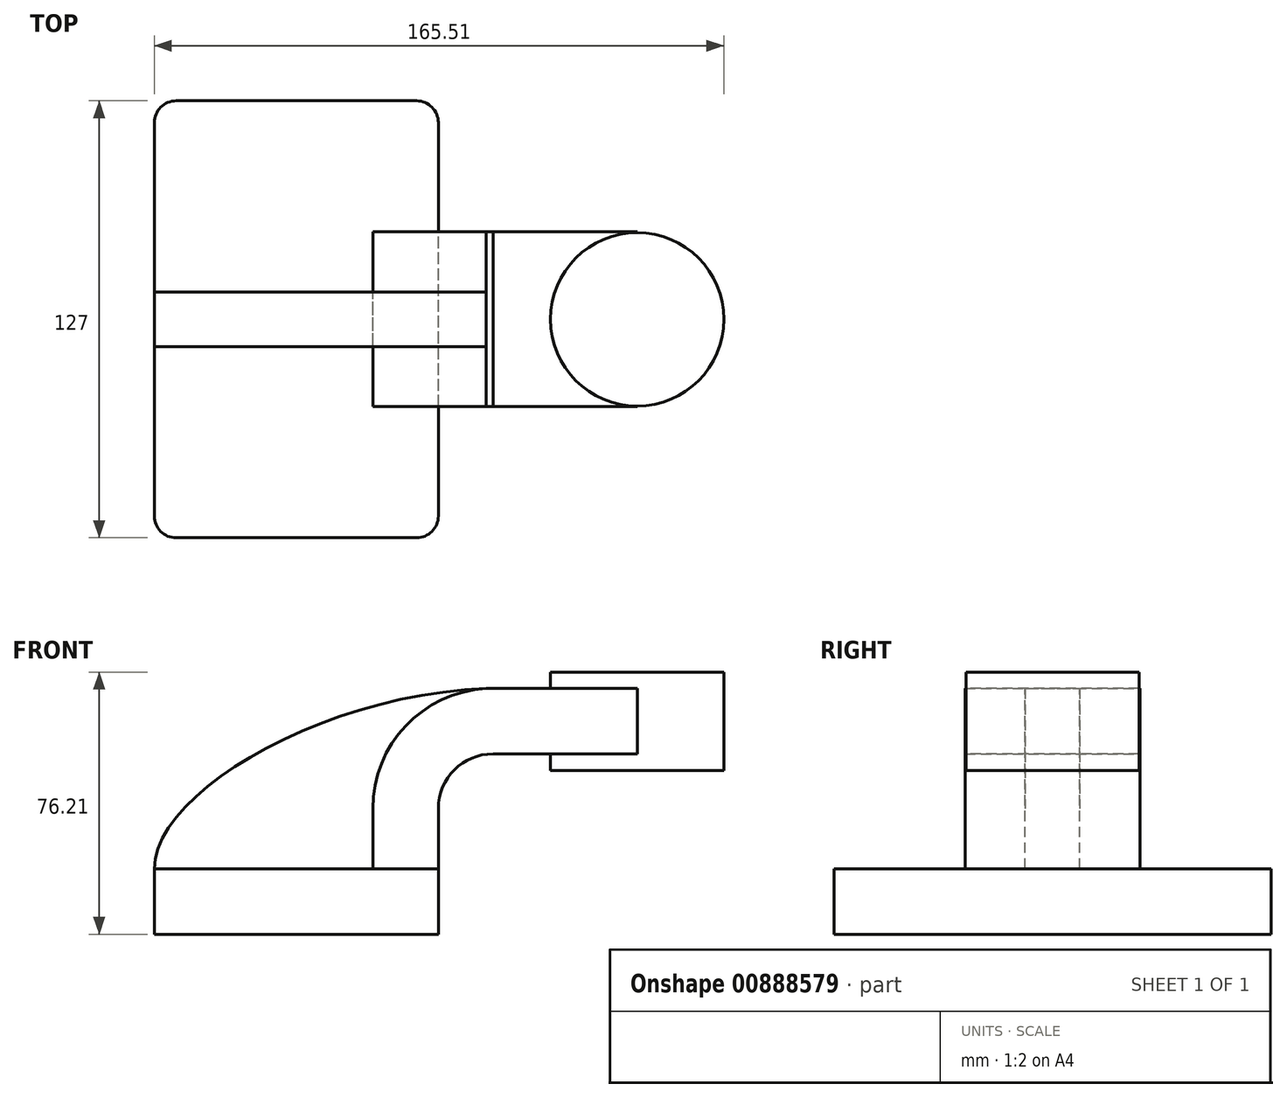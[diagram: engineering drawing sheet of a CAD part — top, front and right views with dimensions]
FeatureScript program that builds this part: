
annotation { "Feature Type Name" : "Feature", "Feature Type Description" : "" }
export const myFeature = defineFeature(function(context is Context, id is Id, definition is map)
    precondition{}
    {
        {
            var Q0;
            Q0=qCreatedBy(makeId("Front.planeOp"),FACE);
            var sketch = newSketch(context, id + "F0", { "sketchPlane" : qUnion([Q0])});
            skLineSegment(sketch, "E0.bottom", {"start": v(-41.28, 9.52) * mm, "end": v(41.27, 9.53) * mm});
            skLineSegment(sketch, "E0.top", {"start": v(-41.28, -9.53) * mm, "end": v(41.28, -9.53) * mm});
            skLineSegment(sketch, "E0.left", {"start": v(-41.28, 9.52) * mm, "end": v(-41.27, -9.53) * mm});
            skLineSegment(sketch, "E0.right", {"start": v(41.28, 9.53) * mm, "end": v(41.28, -9.52) * mm});
            skPoint(sketch, "E0.middle", {"position": v(0, 0) * mm});
            skLineSegment(sketch, "E1.bottom", {"start": v(73.43, 38.1) * mm, "end": v(124.23, 38.1) * mm});
            skLineSegment(sketch, "E1.top", {"start": v(73.43, 66.67) * mm, "end": v(124.23, 66.67) * mm});
            skLineSegment(sketch, "E1.left", {"start": v(73.43, 38.1) * mm, "end": v(73.43, 66.67) * mm});
            skLineSegment(sketch, "E1.right", {"start": v(124.23, 38.1) * mm, "end": v(124.23, 66.67) * mm});
            skPoint(sketch, "E1.middle", {"position": v(98.83, 52.39) * mm});
            skLineSegment(sketch, "E2", {"start": v(41.27, 9.53) * mm, "end": v(41.27, 27) * mm});
            skArc(sketch, "E3", {"start": v(41.27, 27) * mm, "mid": v(45.92, 38.23) * mm, "end": v(57.15, 42.88) * mm});
            skLineSegment(sketch, "E4", {"start": v(57.15, 42.88) * mm, "end": v(99.04, 42.88) * mm});
            skLineSegment(sketch, "E5.0", {"start": v(57.15, 61.93) * mm, "end": v(99.04, 61.93) * mm});
            skArc(sketch, "E5.1", {"start": v(22.22, 27) * mm, "mid": v(32.45, 51.7) * mm, "end": v(57.15, 61.93) * mm});
            skLineSegment(sketch, "E5.2", {"start": v(22.22, 9.53) * mm, "end": v(22.22, 27) * mm});
            skLineSegment(sketch, "E6", {"start": v(99.04, 66.67) * mm, "end": v(99.04, 38.1) * mm});
            skFitSpline(sketch, "E7", {"points": [v(-41.28, 9.52) * mm, v(57.15, 61.93) * mm], "startDerivative": vector(0.2, 66.62) * mm, "endDerivative": vector(146.2, 3.05) * mm});
            skSolve(sketch);
        }
        {
            var Q0;
            Q0=makeQuery(id+"F0.imprint","IMPRINT",FACE,{"disambiguationData":[TD([[makeQuery(id+"F0.imprint","IMPRINT",EDGE,{"derivedFrom":sQuery(id+"F0.wireOp",EDGE,"E0.top")}),1.0]])]});
            extrude(context, id + "F1", {"entities" : qUnion([Q0]), "endBound" : BoundingType.SYMMETRIC, "depth" : 127 * mm, "offsetDistance" : 25.4 * mm});
        }
        {
            var Q0;
            {var subQ1=sQuery(id+"F0.wireOp",EDGE,"E2");Q0=makeQuery(id+"F0.imprint","IMPRINT",FACE,{"disambiguationData":[TD([[makeQuery(id+"F0.imprint","IMPRINT",EDGE,{"derivedFrom":subQ1}),1.0]])]});}
            var Q1;
            {var subQ0=sQuery(id+"F0.wireOp",EDGE,"E4");var subQ1=sQuery(id+"F0.wireOp",EDGE,"E1.left");var subQ2=makeQuery(id+"F0.imprint","INTERSECT",VERTEX,{"derivedFrom":[subQ1,subQ0]});Q1=makeQuery(id+"F0.imprint","IMPRINT",FACE,{"disambiguationData":[TD([[makeQuery(id+"F0.imprint","IMPRINT",EDGE,{"disambiguationData":[TD([[subQ2,-1.0]])],"derivedFrom":subQ1}),-1.0]])]});}
            extrude(context, id + "F2", {"entities" : qUnion([Q0, Q1]), "endBound" : BoundingType.SYMMETRIC, "depth" : 50.8 * mm, "offsetDistance" : 25.4 * mm});
        }
        {
            var Q0;
            {var subQ3=sQuery(id+"F0.wireOp",EDGE,"E5.2");Q0=makeQuery(id+"F0.imprint","IMPRINT",FACE,{"disambiguationData":[TD([[makeQuery(id+"F0.imprint","IMPRINT",EDGE,{"derivedFrom":subQ3}),1.0]])]});}
            extrude(context, id + "F3", {"entities" : qUnion([Q0]), "endBound" : BoundingType.SYMMETRIC, "depth" : 15.88 * mm, "offsetDistance" : 25.4 * mm});
        }
        {
            var Q0;
            {var subQ4=sQuery(id+"F0.wireOp",EDGE,"E1.right");Q0=makeQuery(id+"F0.imprint","IMPRINT",FACE,{"disambiguationData":[TD([[makeQuery(id+"F0.imprint","IMPRINT",EDGE,{"derivedFrom":subQ4}),1.0]])]});}
            var Q1;
            Q1=sQuery(id+"F0.wireOp",EDGE,"E6");
            revolve(context, id + "F4", {"operationType" : NewBodyOperationType.ADD, "surfaceOperationType" : NewSurfaceOperationType.NEW, "entities" : qUnion([Q0]), "axis" : qUnion([Q1]), "revolveType" : RevolveType.FULL});
        }
        {
            var Q0;
            Q0=makeQuery(id+"F1.opExtrude","CAP_EDGE",EDGE,{"disambiguationData":[OSD([sQuery(id+"F0.wireOp",EDGE,"E0.left")])],"isStart":false});
            var Q1;
            Q1=makeQuery(id+"F1.opExtrude","CAP_EDGE",EDGE,{"disambiguationData":[OSD([sQuery(id+"F0.wireOp",EDGE,"E0.right")])],"isStart":false});
            var Q2;
            Q2=makeQuery(id+"F1.opExtrude","CAP_EDGE",EDGE,{"disambiguationData":[OSD([sQuery(id+"F0.wireOp",EDGE,"E0.right")])],"isStart":true});
            var Q3;
            Q3=makeQuery(id+"F1.opExtrude","CAP_EDGE",EDGE,{"disambiguationData":[OSD([sQuery(id+"F0.wireOp",EDGE,"E0.left")])],"isStart":true});
            fillet(context, id + "F5", {"entities" : qUnion([Q0, Q1, Q2, Q3]), "radius" : 6.35 * mm, "tangentPropagation" : true, "allowEdgeOverflow" : false});
        }
    });
